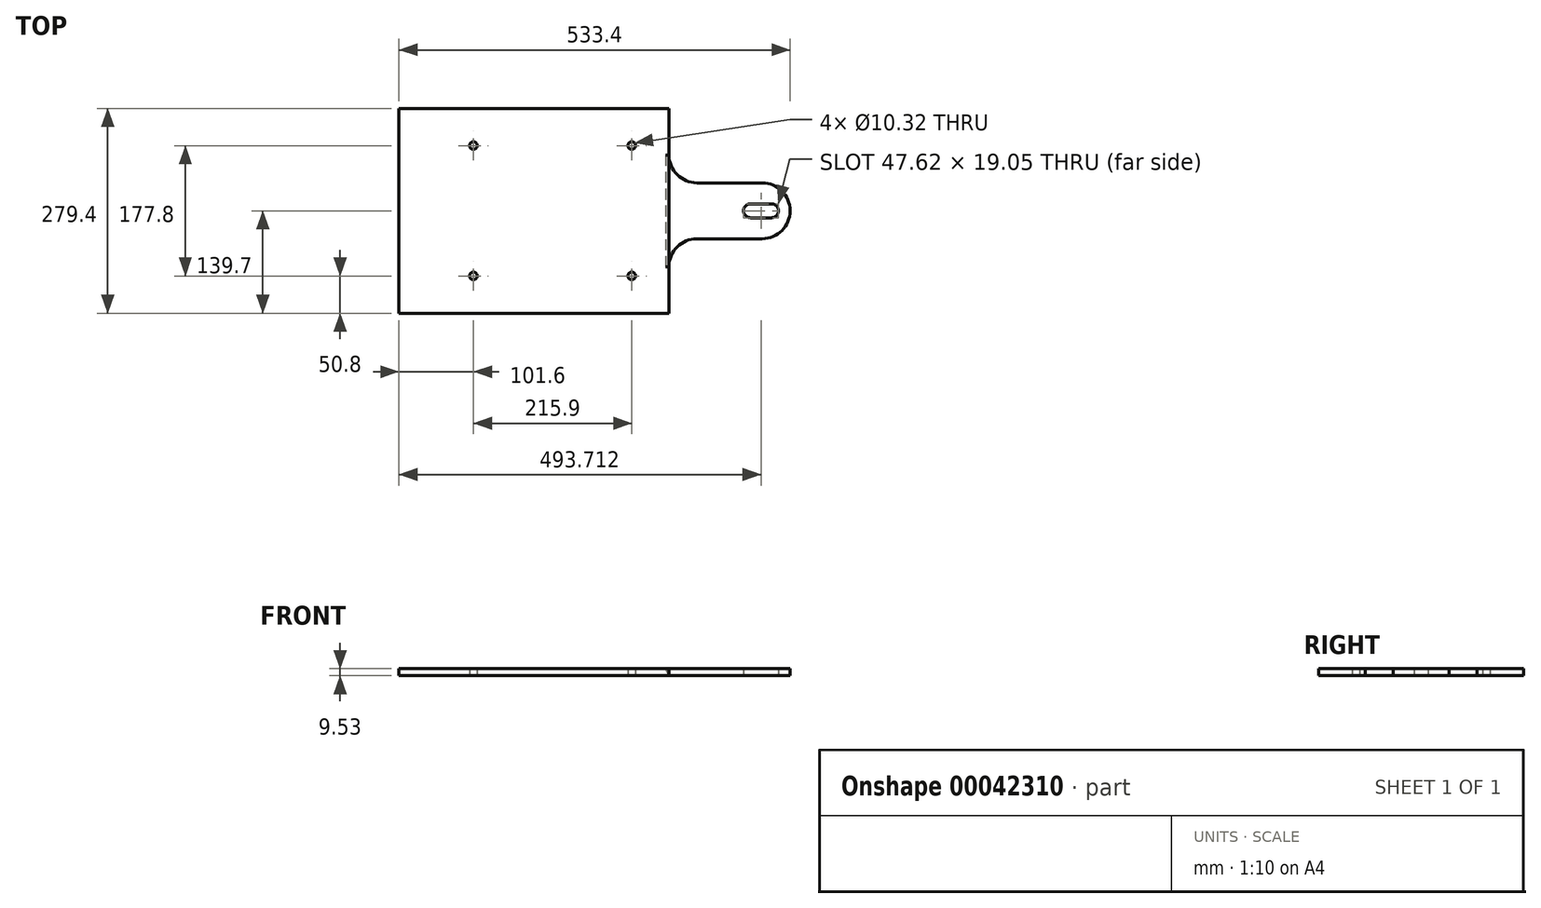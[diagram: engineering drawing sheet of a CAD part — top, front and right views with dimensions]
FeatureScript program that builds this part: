
annotation { "Feature Type Name" : "Feature", "Feature Type Description" : "" }
export const myFeature = defineFeature(function(context is Context, id is Id, definition is map)
    precondition{}
    {
        {
            var Q0;
            Q0=qCreatedBy(makeId("Top.planeOp"),FACE);
            var sketch = newSketch(context, id + "F0", { "sketchPlane" : qUnion([Q0])});
            skLineSegment(sketch, "E0.rect.bottom", {"start": v(101.6, -139.7) * mm, "end": v(-266.7, -139.7) * mm});
            skLineSegment(sketch, "E0.rect.top", {"start": v(101.6, 139.7) * mm, "end": v(-266.7, 139.7) * mm});
            skLineSegment(sketch, "E0.rect.right", {"start": v(-266.7, -139.7) * mm, "end": v(-266.7, 139.7) * mm});
            skPoint(sketch, "E0.rect.middle", {"position": v(0, 0) * mm});
            skLineSegment(sketch, "E1", {"start": v(-165.1, 139.7) * mm, "end": v(-165.1, -139.7) * mm, "construction": true});
            skLineSegment(sketch, "E2", {"start": v(50.8, 139.7) * mm, "end": v(50.8, -139.7) * mm, "construction": true});
            skLineSegment(sketch, "E3", {"start": v(101.6, 139.7) * mm, "end": v(101.6, -139.7) * mm});
            skLineSegment(sketch, "E4", {"start": v(-266.7, 0) * mm, "end": v(266.7, 0) * mm, "construction": true});
            skLineSegment(sketch, "E5", {"start": v(228.6, 38.1) * mm, "end": v(139.7, 38.1) * mm});
            skLineSegment(sketch, "E6.MirrorCS", {"start": v(228.6, -38.1) * mm, "end": v(139.7, -38.1) * mm});
            skLineSegment(sketch, "E7", {"start": v(241.3, 0) * mm, "end": v(212.73, 0) * mm});
            skLineSegment(sketch, "E8", {"start": v(-266.7, 88.9) * mm, "end": v(101.6, 88.9) * mm, "construction": true});
            skLineSegment(sketch, "E9.MirrorCS", {"start": v(-266.7, -88.9) * mm, "end": v(101.6, -88.9) * mm, "construction": true});
            skPoint(sketch, "E10", {"position": v(-165.1, 88.9) * mm});
            skPoint(sketch, "E11", {"position": v(-165.1, -88.9) * mm});
            skPoint(sketch, "E12", {"position": v(50.8, 88.9) * mm});
            skPoint(sketch, "E13", {"position": v(50.8, -88.9) * mm});
            skArc(sketch, "E14.0.startCap", {"start": v(241.3, 9.53) * mm, "mid": v(250.83, 0) * mm, "end": v(241.3, -9.52) * mm});
            skArc(sketch, "E14.0.endCap", {"start": v(212.73, -9.52) * mm, "mid": v(203.2, 0) * mm, "end": v(212.73, 9.53) * mm});
            skLineSegment(sketch, "E14.0.left", {"start": v(241.3, -9.52) * mm, "end": v(212.73, -9.52) * mm});
            skLineSegment(sketch, "E14.0.right", {"start": v(241.3, 9.53) * mm, "end": v(212.73, 9.53) * mm});
            skLineSegment(sketch, "E15", {"start": v(266.7, 0) * mm, "end": v(228.6, 0) * mm, "construction": true});
            skArc(sketch, "E16", {"start": v(228.6, 38.1) * mm, "mid": v(266.7, 0) * mm, "end": v(228.6, -38.1) * mm});
            skPoint(sketch, "E17.orphan", {"position": v(266.7, 38.1) * mm});
            skPoint(sketch, "E18.orphan", {"position": v(266.7, -38.1) * mm});
            skPoint(sketch, "E19", {"position": v(139.7, -76.2) * mm});
            skPoint(sketch, "E20.MirrorP", {"position": v(139.7, 76.2) * mm});
            skArc(sketch, "E21", {"start": v(139.7, -38.1) * mm, "mid": v(112.76, -49.26) * mm, "end": v(101.6, -76.2) * mm});
            skArc(sketch, "E22", {"start": v(139.7, 38.1) * mm, "mid": v(112.76, 49.26) * mm, "end": v(101.6, 76.2) * mm});
            skPoint(sketch, "E23.orphan", {"position": v(101.6, 38.1) * mm});
            skPoint(sketch, "E24.orphan", {"position": v(101.6, -38.1) * mm});
            skPoint(sketch, "E25.orphan", {"position": v(266.7, -139.7) * mm});
            skPoint(sketch, "E26.orphan", {"position": v(266.7, 139.7) * mm});
            skSolve(sketch);
        }
        {
            var Q0;
            {var subQ3=sQuery(id+"F0.wireOp",EDGE,"E0.rect.bottom");Q0=makeQuery(id+"F0.imprint","IMPRINT",FACE,{"disambiguationData":[TD([[makeQuery(id+"F0.imprint","IMPRINT",EDGE,{"derivedFrom":subQ3}),-1.0]])]});}
            extrude(context, id + "F1", {"entities" : qUnion([Q0]), "depth" : 9.52 * mm});
        }
        {
            var Q0;
            Q0=makeQuery(id+"F0.imprint","IMPRINT",FACE,{"disambiguationData":[TD([[makeQuery(id+"F0.imprint","IMPRINT",EDGE,{"derivedFrom":sQuery(id+"F0.wireOp",EDGE,"E5")}),1.0]])]});
            extrude(context, id + "F2", {"entities" : qUnion([Q0]), "depth" : 9.52 * mm});
        }
        {
            var Q0;
            Q0=makeQuery(id+"F2.opExtrude","SWEPT_FACE",FACE,{"disambiguationData":[OSD([sQuery(id+"F0.wireOp",EDGE,"E3")])]});
            var Q1;
            Q1=sQuery(id+"F0.wireOp",EDGE,"E3");
            revolve(context, id + "F3", {"entities" : qUnion([Q0]), "axis" : qUnion([Q1]), "revolveType" : RevolveType.ONE_DIRECTION, "angle" : 30 * degree});
        }
        {
            var Q0;
            Q0=sQuery(id+"F0.wireOp",VERTEX,"E10");
            var Q1;
            Q1=sQuery(id+"F0.wireOp",VERTEX,"E11");
            var Q2;
            Q2=sQuery(id+"F0.wireOp",VERTEX,"E13");
            var Q3;
            Q3=sQuery(id+"F0.wireOp",VERTEX,"E12");
            var Q4;
            Q4=makeQuery(id+"F1.opExtrude","SWEPT_BODY",BODY,{"disambiguationData":[OSD([sQuery(id+"F0.wireOp",EDGE,"E0.rect.bottom"),sQuery(id+"F0.wireOp",EDGE,"E0.rect.top"),sQuery(id+"F0.wireOp",EDGE,"E0.rect.right"),sQuery(id+"F0.wireOp",EDGE,"E3")])]});
            hole(context, id + "F4", {"style" : HoleStyle.SIMPLE, "holeDiameter" : 10.32 * mm, "endStyle" : HoleEndStyle.THROUGH, "oppositeDirection" : true, "locations" : qUnion([Q0, Q1, Q2, Q3]), "scope" : qUnion([Q4])});
        }
    });
